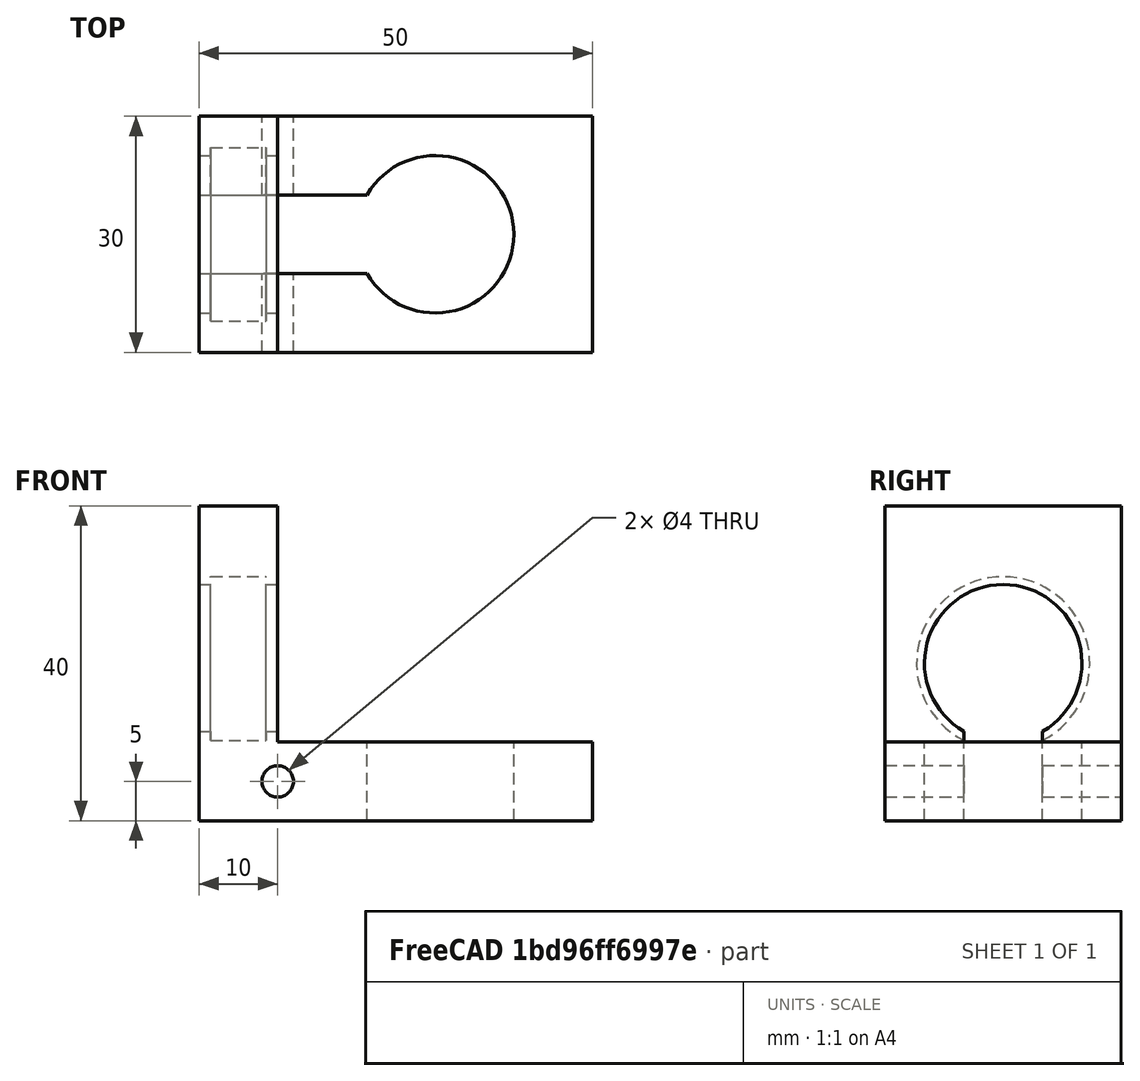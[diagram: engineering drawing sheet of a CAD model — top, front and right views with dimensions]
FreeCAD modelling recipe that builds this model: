
FCSTD DOCUMENT  (FreeCAD 0.17R13522 (Git))
Label: fastener-l-bearing-displaced
License: All rights reserved
LicenseURL: http://en.wikipedia.org/wiki/All_rights_reserved
objects: Part::Cylinder×4, Part::Box×3, Part::MultiFuse×2, Part::Cut×1
note: 10 computed .brp shape members not serialized (recipe doc carries the construction recipe); baked Part::Feature solids carry a one-line shape summary decoded from their .brp

FEATURE [Part::Cylinder] Cylinder001
  Angle = 360
  AttacherType = Attacher::AttachEngine3D
  Height = 30
  Placement = pos=(-20,-15,0) rot=(-1,0,0;1.5708rad)
  Radius = 2
FEATURE [Part::Box] Box  label="Cube"
  AttacherType = Attacher::AttachEngine3D
  Height = 10
  Length = 40
  Placement = pos=(-20,-15,-5) rot=(0,0,1;0rad)
  Width = 30
FEATURE [Part::Cylinder] Cylinder
  Angle = 360
  AttacherType = Attacher::AttachEngine3D
  Height = 10
  Placement = pos=(0,0,-5) rot=(0,0,1;0rad)
  Radius = 10
FEATURE [Part::Box] Box001  label="Cube001"
  AttacherType = Attacher::AttachEngine3D
  Height = 15
  Length = 25
  Placement = pos=(-30,-5,-5) rot=(0,0,1;0rad)
  Width = 10
FEATURE [Part::Box] Box002  label="Cube002"
  AttacherType = Attacher::AttachEngine3D
  Height = 40
  Length = 10
  Placement = pos=(-30,-15,-5) rot=(0,0,1;0rad)
  Width = 30
FEATURE [Part::Cylinder] Cylinder002  label="Bearing Cylinder"
  Angle = 360
  AttacherType = Attacher::AttachEngine3D
  Height = 7
  Placement = pos=(-28.5,0,15) rot=(0,1,0;1.5708rad)
  Radius = 11
FEATURE [Part::MultiFuse] Fusion001  label="Positive Fusion"
  Shapes = -> [Box,Box002]
FEATURE [Part::Cylinder] Cylinder003  label="Bearing Cylinder Outer"
  Angle = 360
  AttacherType = Attacher::AttachEngine3D
  Height = 10
  Placement = pos=(-30,0,15) rot=(0,1,0;1.5708rad)
  Radius = 10
FEATURE [Part::MultiFuse] Fusion  label="Negative Fusion"
  Shapes = -> [Box001,Cylinder,Cylinder001,Cylinder002,Cylinder003]
FEATURE [Part::Cut] Cut
  Base = -> Fusion001
  Tool = -> Fusion
